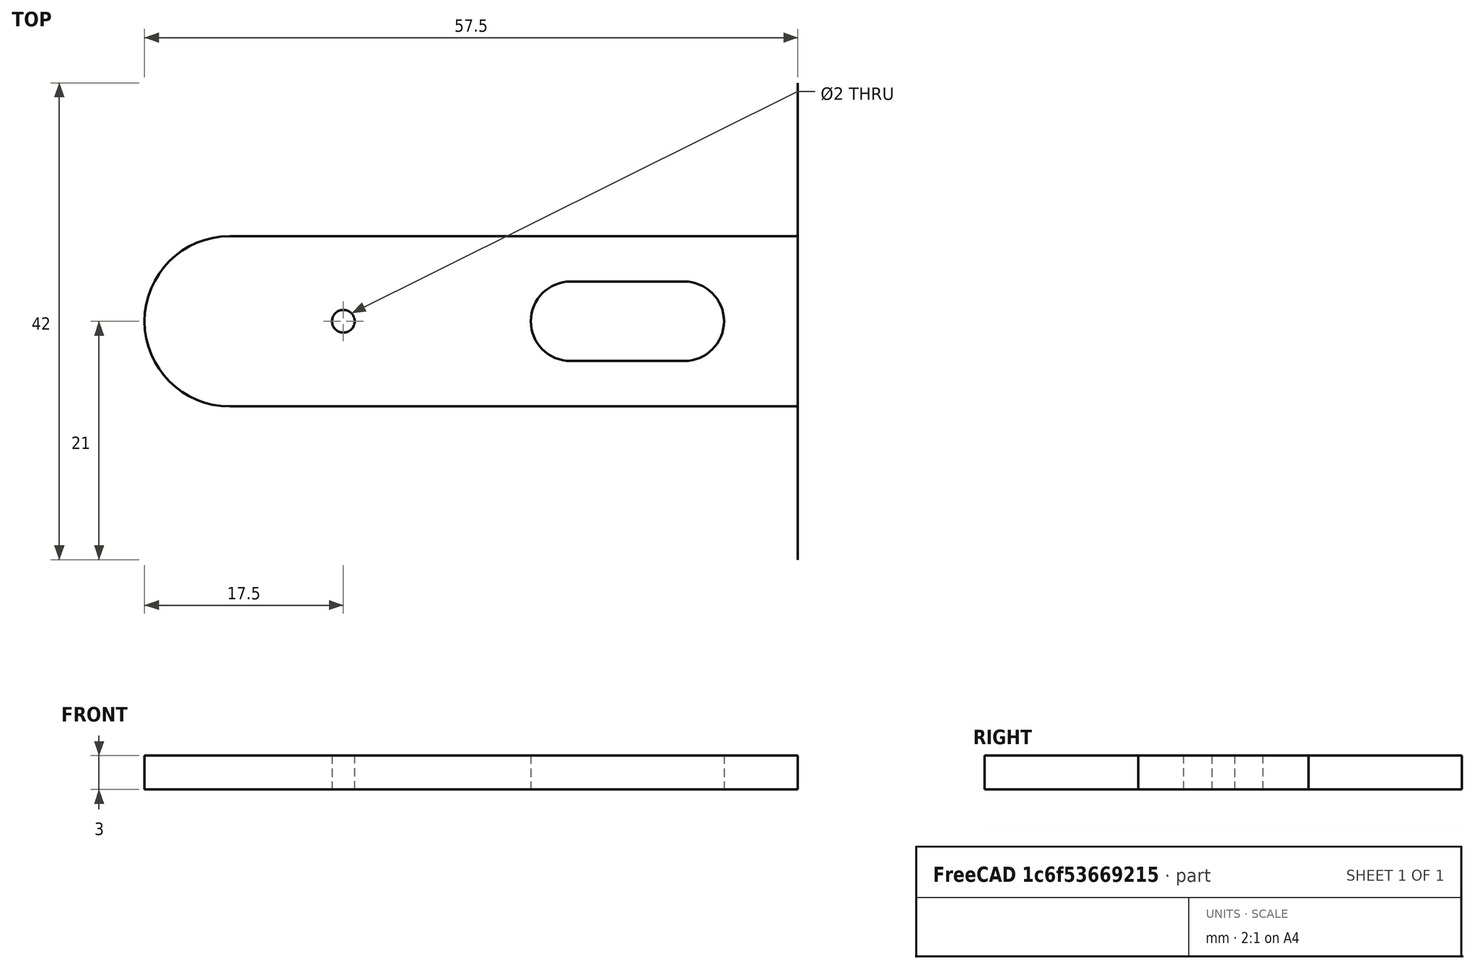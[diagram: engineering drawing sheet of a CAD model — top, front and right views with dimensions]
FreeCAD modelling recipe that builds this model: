
FCSTD DOCUMENT  (FreeCAD 0.18R4 (GitTag))
Label: Arm
License: All rights reserved
LicenseURL: http://en.wikipedia.org/wiki/All_rights_reserved
objects: Sketcher::SketchObject×1, Part::Extrusion×1
note: 2 computed .brp shape members not serialized (recipe doc carries the construction recipe); baked Part::Feature solids carry a one-line shape summary decoded from their .brp

FEATURE [Sketcher::SketchObject] Sketch
  sketch-geometry (9):
    g0: LineSegment StartX=40 StartY=21 StartZ=0 EndX=40 EndY=-21 EndZ=0
    g1: ArcOfCircle CenterX=-10 CenterY=1.45e-13 CenterZ=0 NormalX=0 NormalY=0 NormalZ=1 AngleXU=0 Radius=7.5 StartAngle=1.5708 EndAngle=4.71239
    g2: LineSegment StartX=40 StartY=7.5 StartZ=0 EndX=-10 EndY=7.5 EndZ=0
    g3: LineSegment StartX=40 StartY=-7.5 StartZ=0 EndX=-10 EndY=-7.5 EndZ=0
    g4: Circle CenterX=0 CenterY=0 CenterZ=0 NormalX=0 NormalY=0 NormalZ=1 AngleXU=0 Radius=1
    g5: ArcOfCircle CenterX=30 CenterY=1e-16 CenterZ=0 NormalX=0 NormalY=0 NormalZ=1 AngleXU=0 Radius=3.5 StartAngle=4.71239 EndAngle=7.85398
    g6: ArcOfCircle CenterX=20 CenterY=-1.06e-14 CenterZ=0 NormalX=0 NormalY=0 NormalZ=1 AngleXU=0 Radius=3.5 StartAngle=1.5708 EndAngle=4.71239
    g7: LineSegment StartX=30 StartY=3.5 StartZ=0 EndX=20 EndY=3.5 EndZ=0
    g8: LineSegment StartX=30 StartY=-3.5 StartZ=0 EndX=20 EndY=-3.5 EndZ=0
  constraints (22):
    c: DistanceY(g0,g0) = 42
    c: Symmetric(g0,g0,g-1)
    c: Tangent(g2,g1) = -1.5708
    c: Tangent(g3,g1) = 1.5708
    c: Horizontal(g2)
    c: DistanceX(g-1,g0) = 40
    c: DistanceY(g1,g1) = 15
    c: Symmetric(g1,g1,g-1)
    c: Equal(g3,g2)
    c: DistanceX(g1,g3) = 50
    c: PointOnObject(g2,g0)
    c: Radius(g4) = 1
    c: Coincident(g4,g-1)
    c: Tangent(g5,g8) = 1.5708
    c: Tangent(g5,g7) = -1.5708
    c: Tangent(g7,g6) = -1.5708
    c: Tangent(g8,g6) = 1.5708
    c: Horizontal(g7)
    c: DistanceY(g6,g6) = 7
    c: DistanceX(g6,g5) = 10
    c: Symmetric(g5,g5,g-1)
    c: DistanceX(g4,g6) = 20
FEATURE [Part::Extrusion] Extrude
  Base = -> Sketch
  Dir = (0,0,1)
  DirMode = 2
  FaceMakerClass = Part::FaceMakerBullseye
  LengthFwd = 3
  LengthRev = 0
  Solid = false
  Symmetric = false
